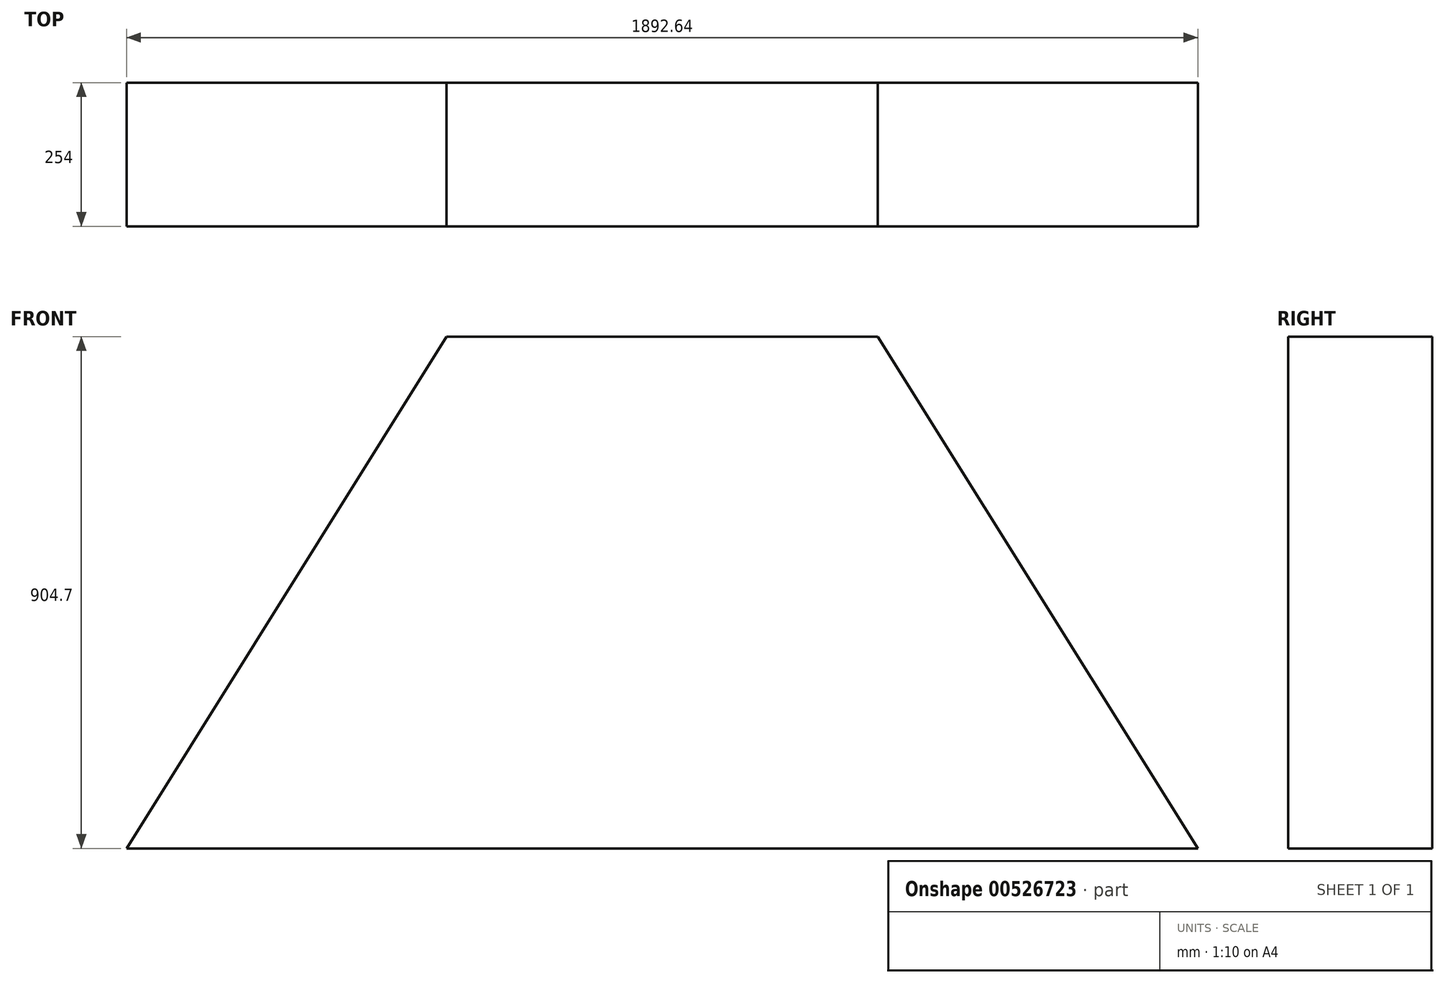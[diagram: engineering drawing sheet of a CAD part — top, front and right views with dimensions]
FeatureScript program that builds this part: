
annotation { "Feature Type Name" : "Feature", "Feature Type Description" : "" }
export const myFeature = defineFeature(function(context is Context, id is Id, definition is map)
    precondition{}
    {
        {
            var Q0;
            Q0=qCreatedBy(makeId("Front.planeOp"),FACE);
            var sketch = newSketch(context, id + "F0", { "sketchPlane" : qUnion([Q0])});
            skLineSegment(sketch, "E0", {"start": v(-139.36, 0) * mm, "end": v(1892.64, 0) * mm});
            skLineSegment(sketch, "E1", {"start": v(1892.64, 0) * mm, "end": v(1327.32, 904.7) * mm});
            skLineSegment(sketch, "E2", {"start": v(0, 0) * mm, "end": v(565.32, 904.7) * mm});
            skLineSegment(sketch, "E3", {"start": v(565.32, 904.7) * mm, "end": v(1327.32, 904.7) * mm});
            skSolve(sketch);
        }
        {
            var Q0;
            {var subQ0=sQuery(id+"F0.wireOp",EDGE,"E1");Q0=makeQuery(id+"F0.imprint","IMPRINT",FACE,{"disambiguationData":[TD([[makeQuery(id+"F0.imprint","IMPRINT",EDGE,{"derivedFrom":subQ0}),1.0]])]});}
            extrude(context, id + "F1", {"entities" : qUnion([Q0]), "depth" : 254 * mm, "offsetDistance" : 25.4 * mm});
        }
    });
